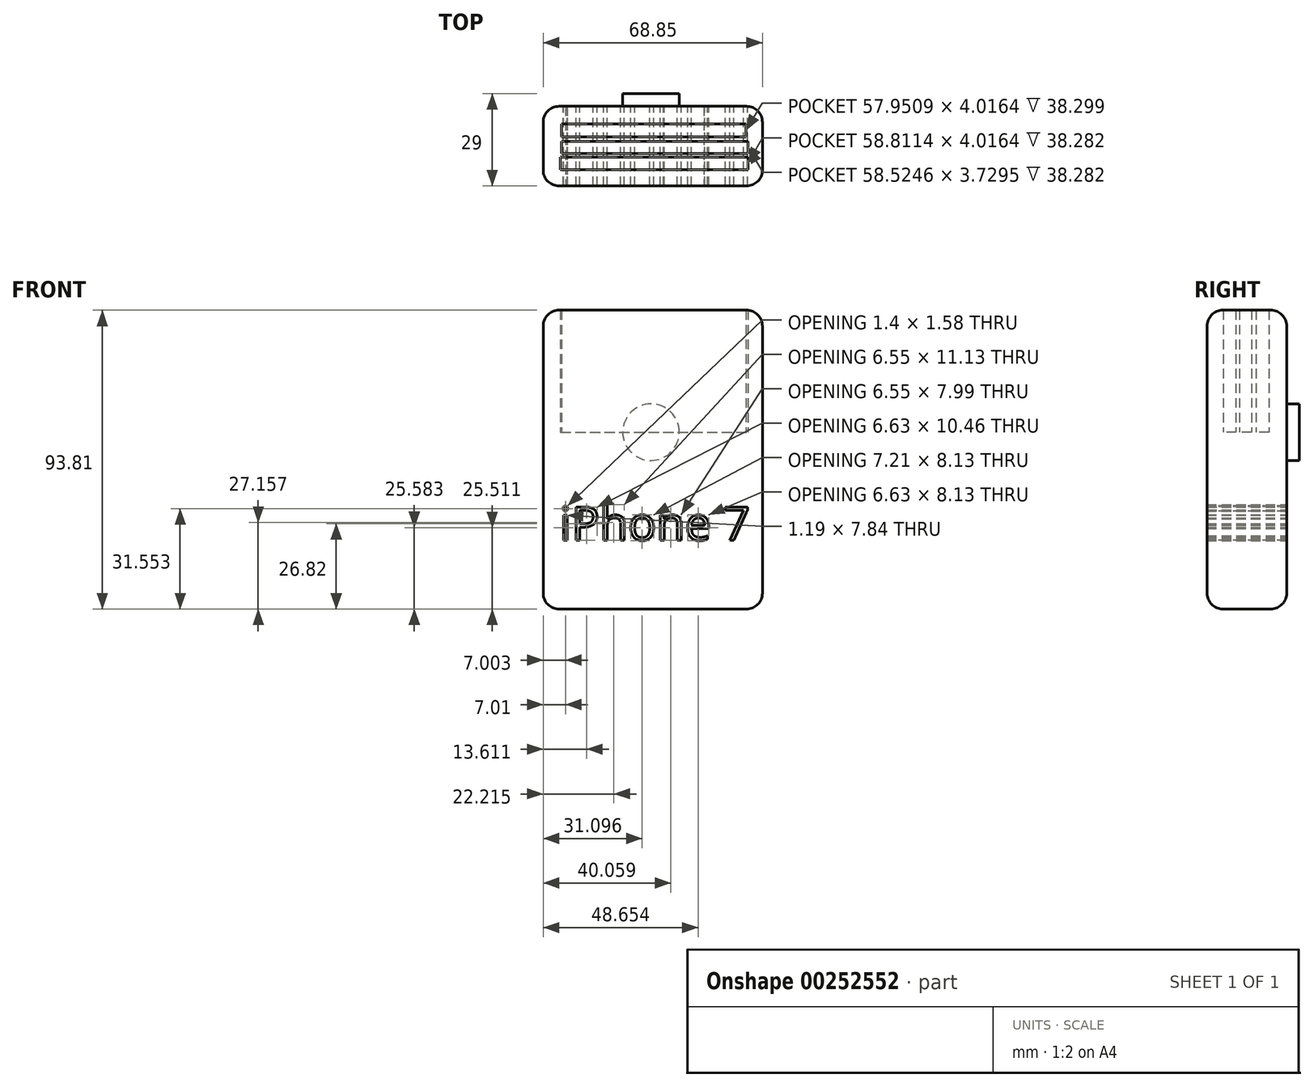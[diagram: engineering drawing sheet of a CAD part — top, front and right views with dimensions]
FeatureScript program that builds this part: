
annotation { "Feature Type Name" : "Feature", "Feature Type Description" : "" }
export const myFeature = defineFeature(function(context is Context, id is Id, definition is map)
    precondition{}
    {
        {
            var Q0;
            Q0=qCreatedBy(makeId("Front.planeOp"),FACE);
            var sketch = newSketch(context, id + "F0", { "sketchPlane" : qUnion([Q0])});
            skLineSegment(sketch, "E0.bottom", {"start": v(-33.85, 38.3) * mm, "end": v(35, 38.3) * mm});
            skLineSegment(sketch, "E0.top", {"start": v(-33.85, -55.51) * mm, "end": v(35, -55.51) * mm});
            skLineSegment(sketch, "E0.left", {"start": v(-33.85, 38.3) * mm, "end": v(-33.85, -55.51) * mm});
            skLineSegment(sketch, "E0.right", {"start": v(35, 38.3) * mm, "end": v(35, -55.51) * mm});
            skSolve(sketch);
        }
        {
            var Q0;
            Q0 = qSketchRegion(id + "F0", true);
            extrude(context, id + "F1", {"entities" : qUnion([Q0]), "depth" : 25 * mm});
        }
        {
            var Q0;
            Q0=makeQuery(id+"F1.opExtrude","SWEPT_EDGE",EDGE,{"disambiguationData":[OSD([sQuery(id+"F0.wireOp",EDGE,"E0.bottom"),sQuery(id+"F0.wireOp",EDGE,"E0.right")])]});
            var Q1;
            Q1=makeQuery(id+"F1.opExtrude","CAP_EDGE",EDGE,{"disambiguationData":[OSD([sQuery(id+"F0.wireOp",EDGE,"E0.bottom")])],"isStart":true});
            var Q2;
            Q2=makeQuery(id+"F1.opExtrude","SWEPT_EDGE",EDGE,{"disambiguationData":[OSD([sQuery(id+"F0.wireOp",EDGE,"E0.bottom"),sQuery(id+"F0.wireOp",EDGE,"E0.left")])]});
            var Q3;
            Q3=makeQuery(id+"F1.opExtrude","CAP_EDGE",EDGE,{"disambiguationData":[OSD([sQuery(id+"F0.wireOp",EDGE,"E0.bottom")])],"isStart":false});
            var Q4;
            Q4=makeQuery(id+"F1.opExtrude","CAP_EDGE",EDGE,{"disambiguationData":[OSD([sQuery(id+"F0.wireOp",EDGE,"E0.left")])],"isStart":true});
            var Q5;
            Q5=makeQuery(id+"F1.opExtrude","CAP_EDGE",EDGE,{"disambiguationData":[OSD([sQuery(id+"F0.wireOp",EDGE,"E0.right")])],"isStart":true});
            var Q6;
            Q6=makeQuery(id+"F1.opExtrude","CAP_EDGE",EDGE,{"disambiguationData":[OSD([sQuery(id+"F0.wireOp",EDGE,"E0.top")])],"isStart":true});
            var Q7;
            Q7=makeQuery(id+"F1.opExtrude","CAP_EDGE",EDGE,{"disambiguationData":[OSD([sQuery(id+"F0.wireOp",EDGE,"E0.left")])],"isStart":false});
            var Q8;
            Q8=makeQuery(id+"F1.opExtrude","CAP_EDGE",EDGE,{"disambiguationData":[OSD([sQuery(id+"F0.wireOp",EDGE,"E0.right")])],"isStart":false});
            var Q9;
            Q9=makeQuery(id+"F1.opExtrude","CAP_EDGE",EDGE,{"disambiguationData":[OSD([sQuery(id+"F0.wireOp",EDGE,"E0.top")])],"isStart":false});
            var Q10;
            Q10=makeQuery(id+"F1.opExtrude","SWEPT_EDGE",EDGE,{"disambiguationData":[OSD([sQuery(id+"F0.wireOp",EDGE,"E0.top"),sQuery(id+"F0.wireOp",EDGE,"E0.left")])]});
            var Q11;
            Q11=makeQuery(id+"F1.opExtrude","SWEPT_EDGE",EDGE,{"disambiguationData":[OSD([sQuery(id+"F0.wireOp",EDGE,"E0.top"),sQuery(id+"F0.wireOp",EDGE,"E0.right")])]});
            fillet(context, id + "F2", {"entities" : qUnion([Q0, Q1, Q2, Q3, Q4, Q5, Q6, Q7, Q8, Q9, Q10, Q11]), "radius" : 5 * mm, "tangentPropagation" : true, "allowEdgeOverflow" : false});
        }
        {
            var Q0;
            Q0=qCreatedBy(makeId("Front.planeOp"),FACE);
            var sketch = newSketch(context, id + "F3", { "sketchPlane" : qUnion([Q0])});
            skCircle(sketch, "E1", {"center": v(0, 0) * mm, "radius": 8.88 * mm});
            skSolve(sketch);
        }
        {
            var Q0;
            Q0 = qSketchRegion(id + "F3", true);
            extrude(context, id + "F4", {"entities" : qUnion([Q0]), "operationType" : NewBodyOperationType.ADD, "oppositeDirection" : true, "depth" : 4 * mm});
        }
        {
            var Q0;
            Q0=qCreatedBy(makeId("Top.planeOp"),FACE);
            var sketch = newSketch(context, id + "F5", { "sketchPlane" : qUnion([Q0])});
            skLineSegment(sketch, "E2.bottom", {"start": v(-28.11, -5.6) * mm, "end": v(29.84, -5.6) * mm});
            skLineSegment(sketch, "E2.top", {"start": v(-28.11, -9.61) * mm, "end": v(29.84, -9.61) * mm});
            skLineSegment(sketch, "E2.left", {"start": v(-28.11, -5.6) * mm, "end": v(-28.11, -9.61) * mm});
            skLineSegment(sketch, "E2.right", {"start": v(29.84, -5.6) * mm, "end": v(29.84, -9.61) * mm});
            skSolve(sketch);
        }
        {
            var Q0;
            Q0 = qSketchRegion(id + "F5", true);
            extrude(context, id + "F6", {"entities" : qUnion([Q0]), "operationType" : NewBodyOperationType.REMOVE, "depth" : 680.5 * mm});
        }
        {
            var Q0;
            Q0=qCreatedBy(makeId("Top.planeOp"),FACE);
            var sketch = newSketch(context, id + "F7", { "sketchPlane" : qUnion([Q0])});
            skLineSegment(sketch, "E3.bottom", {"start": v(-28.11, -11.05) * mm, "end": v(30.4, -11.05) * mm});
            skLineSegment(sketch, "E3.top", {"start": v(-28.11, -14.77) * mm, "end": v(30.4, -14.77) * mm});
            skLineSegment(sketch, "E3.left", {"start": v(-28.11, -11.05) * mm, "end": v(-28.11, -14.77) * mm});
            skLineSegment(sketch, "E3.right", {"start": v(30.4, -11.05) * mm, "end": v(30.4, -14.77) * mm});
            skSolve(sketch);
        }
        {
            var Q0;
            Q0=qCreatedBy(makeId("Top.planeOp"),FACE);
            var sketch = newSketch(context, id + "F8", { "sketchPlane" : qUnion([Q0])});
            skLineSegment(sketch, "E4.bottom", {"start": v(-28.4, -15.92) * mm, "end": v(30.4, -15.92) * mm});
            skLineSegment(sketch, "E4.top", {"start": v(-28.4, -19.94) * mm, "end": v(30.4, -19.94) * mm});
            skLineSegment(sketch, "E4.left", {"start": v(-28.4, -15.92) * mm, "end": v(-28.4, -19.94) * mm});
            skLineSegment(sketch, "E4.right", {"start": v(30.4, -15.92) * mm, "end": v(30.4, -19.94) * mm});
            skSolve(sketch);
        }
        {
            var Q0;
            Q0 = qSketchRegion(id + "F7", true);
            var Q1;
            Q1 = qSketchRegion(id + "F8", true);
            extrude(context, id + "F9", {"entities" : qUnion([Q0, Q1]), "operationType" : NewBodyOperationType.REMOVE, "depth" : 1082.6 * mm});
        }
        {
            var Q0;
            Q0=qCreatedBy(makeId("Front.planeOp"),FACE);
            var sketch = newSketch(context, id + "F10", { "sketchPlane" : qUnion([Q0])});
            skText(sketch, "E5", { "text": "iPhone 7", "fontName": "OpenSans-Regular.ttf"});
            const initialGuessF10  = {"E5": [-0.0287, -0.03392, 1, 0, 0.01055]};
            skSetInitialGuess(sketch, initialGuessF10);
            skSolve(sketch);
        }
        {
            var Q0;
            Q0 = qSketchRegion(id + "F10", true);
            extrude(context, id + "F11", {"entities" : qUnion([Q0]), "operationType" : NewBodyOperationType.REMOVE, "depth" : 64.8 * mm});
        }
    });
